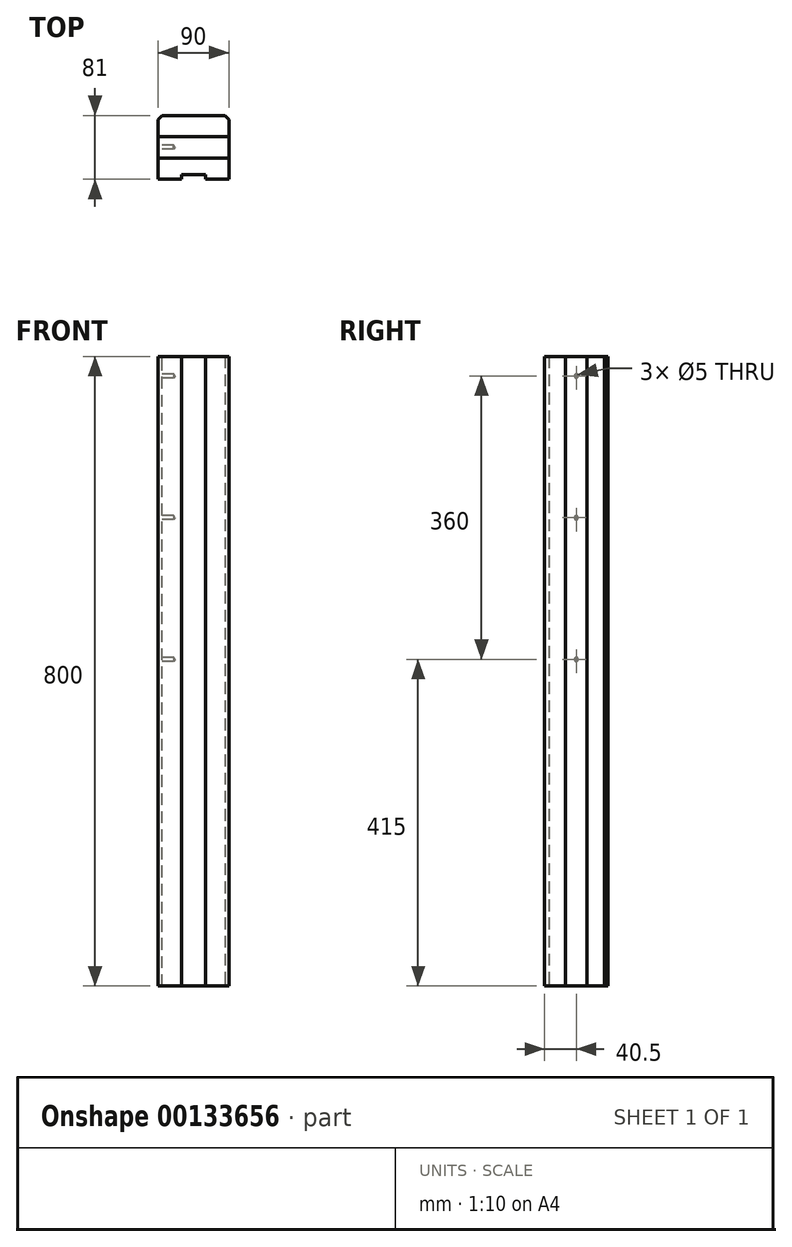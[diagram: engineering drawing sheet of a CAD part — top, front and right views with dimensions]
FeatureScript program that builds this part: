
annotation { "Feature Type Name" : "Feature", "Feature Type Description" : "" }
export const myFeature = defineFeature(function(context is Context, id is Id, definition is map)
    precondition{}
    {
        {
            var Q0;
            Q0=qCreatedBy(makeId("Top.planeOp"),FACE);
            var sketch = newSketch(context, id + "F0", { "sketchPlane" : qUnion([Q0])});
            skLineSegment(sketch, "E0.bottom", {"start": v(45, -13.5) * mm, "end": v(-45, -13.5) * mm});
            skLineSegment(sketch, "E0.top", {"start": v(45, 13.5) * mm, "end": v(-45, 13.5) * mm});
            skLineSegment(sketch, "E0.left", {"start": v(45, -13.5) * mm, "end": v(45, 13.5) * mm});
            skLineSegment(sketch, "E0.right", {"start": v(-45, -13.5) * mm, "end": v(-45, 13.5) * mm});
            skPoint(sketch, "E0.middle", {"position": v(0, 0) * mm});
            skSolve(sketch);
        }
        {
            var Q0;
            Q0=makeQuery(id+"F0.imprint","IMPRINT",FACE,{"disambiguationData":[TD([[makeQuery(id+"F0.imprint","IMPRINT",EDGE,{"derivedFrom":sQuery(id+"F0.wireOp",EDGE,"E0.bottom")}),-1.0]])]});
            extrude(context, id + "F1", {"entities" : qUnion([Q0]), "oppositeDirection" : true, "depth" : 800 * mm});
        }
        {
            var Q0;
            Q0=qCreatedBy(makeId("Top.planeOp"),FACE);
            var sketch = newSketch(context, id + "F2", { "sketchPlane" : qUnion([Q0])});
            skLineSegment(sketch, "E1.bottom", {"start": v(-45, -13.5) * mm, "end": v(45, -13.5) * mm});
            skLineSegment(sketch, "E1.top", {"start": v(-45, -40.5) * mm, "end": v(45, -40.5) * mm});
            skLineSegment(sketch, "E1.left", {"start": v(-45, -13.5) * mm, "end": v(-45, -40.5) * mm});
            skLineSegment(sketch, "E1.right", {"start": v(45, -13.5) * mm, "end": v(45, -40.5) * mm});
            skLineSegment(sketch, "E2.bottom", {"start": v(-45, 13.5) * mm, "end": v(45, 13.5) * mm});
            skLineSegment(sketch, "E2.top", {"start": v(-45, 40.5) * mm, "end": v(45, 40.5) * mm});
            skLineSegment(sketch, "E2.left", {"start": v(-45, 13.5) * mm, "end": v(-45, 40.5) * mm});
            skLineSegment(sketch, "E2.right", {"start": v(45, 13.5) * mm, "end": v(45, 40.5) * mm});
            skSolve(sketch);
        }
        {
            var Q0;
            Q0=makeQuery(id+"F2.imprint","IMPRINT",FACE,{"disambiguationData":[TD([[makeQuery(id+"F2.imprint","IMPRINT",EDGE,{"derivedFrom":sQuery(id+"F2.wireOp",EDGE,"E2.bottom")}),1.0]])]});
            var Q1;
            Q1=makeQuery(id+"F2.imprint","IMPRINT",FACE,{"disambiguationData":[TD([[makeQuery(id+"F2.imprint","IMPRINT",EDGE,{"derivedFrom":sQuery(id+"F2.wireOp",EDGE,"E1.bottom")}),-1.0]])]});
            extrude(context, id + "F3", {"entities" : qUnion([Q0, Q1]), "oppositeDirection" : true, "depth" : 800 * mm});
        }
        {
            var Q0;
            Q0=makeQuery(id+"F3.opExtrude","SWEPT_FACE",FACE,{"disambiguationData":[OSD([sQuery(id+"F2.wireOp",EDGE,"E1.top")])]});
            var sketch = newSketch(context, id + "F4", { "sketchPlane" : qUnion([Q0])});
            skLineSegment(sketch, "E3.bottom", {"start": v(-15.25, 0) * mm, "end": v(15.25, 0) * mm});
            skLineSegment(sketch, "E3.top", {"start": v(-15.25, -800) * mm, "end": v(15.25, -800) * mm});
            skLineSegment(sketch, "E3.left", {"start": v(-15.25, 0) * mm, "end": v(-15.25, -800) * mm});
            skLineSegment(sketch, "E3.right", {"start": v(15.25, 0) * mm, "end": v(15.25, -800) * mm});
            skSolve(sketch);
        }
        {
            var Q0;
            Q0 = qSketchRegion(id + "F4", true);
            extrude(context, id + "F5", {"entities" : qUnion([Q0]), "operationType" : NewBodyOperationType.REMOVE, "oppositeDirection" : true, "depth" : 6 * mm});
        }
        {
            var Q0;
            Q0=makeQuery(id+"F1.opExtrude","SWEPT_FACE",FACE,{"disambiguationData":[OSD([sQuery(id+"F0.wireOp",EDGE,"E0.right")])]});
            var sketch = newSketch(context, id + "F6", { "sketchPlane" : qUnion([Q0])});
            skPoint(sketch, "E4", {"position": v(0, -25) * mm});
            skPoint(sketch, "E5", {"position": v(0, -205) * mm});
            skPoint(sketch, "E6", {"position": v(0, -385) * mm});
            skSolve(sketch);
        }
        {
            var Q0;
            Q0=sQuery(id+"F6.wireOp",VERTEX,"E4");
            var Q1;
            Q1=sQuery(id+"F6.wireOp",VERTEX,"E5");
            var Q2;
            Q2=sQuery(id+"F6.wireOp",VERTEX,"E6");
            var Q3;
            Q3=makeQuery(id+"F1.opExtrude","SWEPT_BODY",BODY,{"disambiguationData":[OSD([sQuery(id+"F0.wireOp",EDGE,"E0.bottom"),sQuery(id+"F0.wireOp",EDGE,"E0.top"),sQuery(id+"F0.wireOp",EDGE,"E0.left"),sQuery(id+"F0.wireOp",EDGE,"E0.right")])]});
            hole(context, id + "F7", {"style" : HoleStyle.SIMPLE, "endStyle" : HoleEndStyle.BLIND, "holeDiameter" : 5 * mm, "holeDepth" : 20 * mm, "startFromSketch" : true, "locations" : qUnion([Q0, Q1, Q2]), "scope" : qUnion([Q3])});
        }
        {
            var Q0;
            Q0=makeQuery(id+"F3.opExtrude","SWEPT_EDGE",EDGE,{"disambiguationData":[OSD([sQuery(id+"F2.wireOp",EDGE,"E2.top"),sQuery(id+"F2.wireOp",EDGE,"E2.right")])]});
            var Q1;
            Q1=makeQuery(id+"F3.opExtrude","SWEPT_EDGE",EDGE,{"disambiguationData":[OSD([sQuery(id+"F2.wireOp",EDGE,"E2.top"),sQuery(id+"F2.wireOp",EDGE,"E2.left")])]});
            chamfer(context, id + "F8", {"entities" : qUnion([Q0, Q1]), "width" : 5 * mm, "tangentPropagation" : true});
        }
    });
